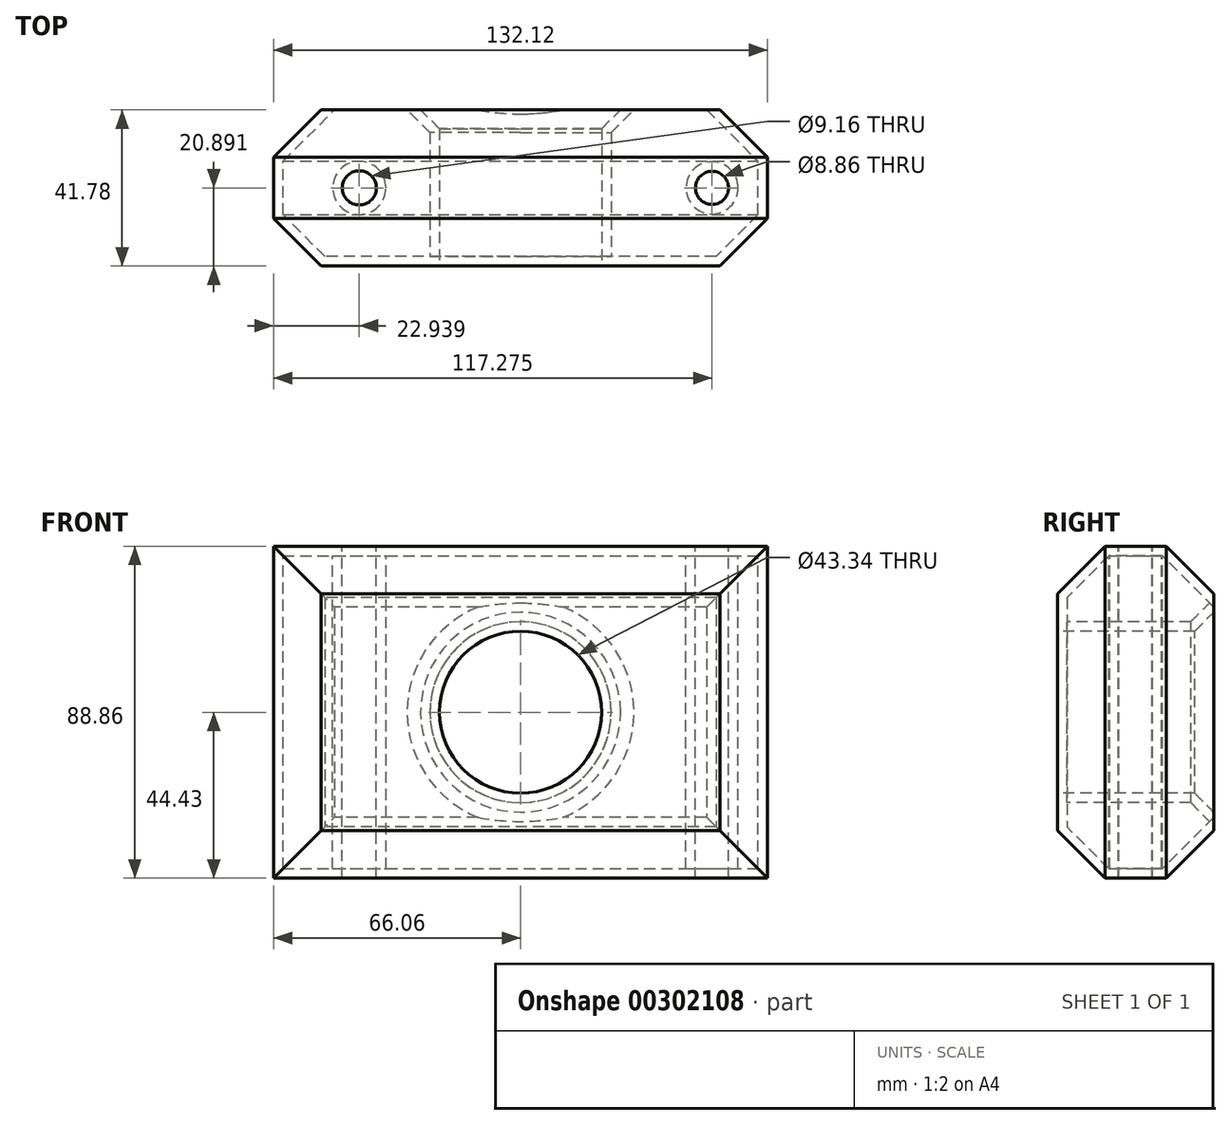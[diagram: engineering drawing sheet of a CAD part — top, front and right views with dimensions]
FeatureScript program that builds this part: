
annotation { "Feature Type Name" : "Feature", "Feature Type Description" : "" }
export const myFeature = defineFeature(function(context is Context, id is Id, definition is map)
    precondition{}
    {
        {
            var Q0;
            Q0=qCreatedBy(makeId("Front.planeOp"),FACE);
            var sketch = newSketch(context, id + "F0", { "sketchPlane" : qUnion([Q0])});
            skLineSegment(sketch, "E0.bottom", {"start": v(66.06, 44.43) * mm, "end": v(-66.06, 44.43) * mm});
            skLineSegment(sketch, "E0.top", {"start": v(66.06, -44.43) * mm, "end": v(-66.06, -44.43) * mm});
            skLineSegment(sketch, "E0.left", {"start": v(66.06, 44.43) * mm, "end": v(66.06, -44.43) * mm});
            skLineSegment(sketch, "E0.right", {"start": v(-66.06, 44.43) * mm, "end": v(-66.06, -44.43) * mm});
            skPoint(sketch, "E0.middle", {"position": v(0, 0) * mm});
            skSolve(sketch);
        }
        {
            var Q0;
            Q0=makeQuery(id+"F0.imprint","IMPRINT",FACE,{"disambiguationData":[TD([[makeQuery(id+"F0.imprint","IMPRINT",EDGE,{"derivedFrom":sQuery(id+"F0.wireOp",EDGE,"E0.bottom")}),1.0]])]});
            extrude(context, id + "F1", {"entities" : qUnion([Q0]), "depth" : 41.78 * mm});
        }
        {
            var Q0;
            Q0=makeQuery(id+"F1.opExtrude","CAP_EDGE",EDGE,{"disambiguationData":[OSD([sQuery(id+"F0.wireOp",EDGE,"E0.top")])],"isStart":false});
            var Q1;
            Q1=makeQuery(id+"F1.opExtrude","CAP_EDGE",EDGE,{"disambiguationData":[OSD([sQuery(id+"F0.wireOp",EDGE,"E0.left")])],"isStart":false});
            var Q2;
            Q2=makeQuery(id+"F1.opExtrude","CAP_EDGE",EDGE,{"disambiguationData":[OSD([sQuery(id+"F0.wireOp",EDGE,"E0.bottom")])],"isStart":false});
            var Q3;
            Q3=makeQuery(id+"F1.opExtrude","CAP_EDGE",EDGE,{"disambiguationData":[OSD([sQuery(id+"F0.wireOp",EDGE,"E0.right")])],"isStart":false});
            var Q4;
            Q4=makeQuery(id+"F1.opExtrude","CAP_EDGE",EDGE,{"disambiguationData":[OSD([sQuery(id+"F0.wireOp",EDGE,"E0.top")])],"isStart":true});
            var Q5;
            Q5=makeQuery(id+"F1.opExtrude","CAP_EDGE",EDGE,{"disambiguationData":[OSD([sQuery(id+"F0.wireOp",EDGE,"E0.left")])],"isStart":true});
            var Q6;
            Q6=makeQuery(id+"F1.opExtrude","CAP_EDGE",EDGE,{"disambiguationData":[OSD([sQuery(id+"F0.wireOp",EDGE,"E0.right")])],"isStart":true});
            var Q7;
            Q7=makeQuery(id+"F1.opExtrude","CAP_EDGE",EDGE,{"disambiguationData":[OSD([sQuery(id+"F0.wireOp",EDGE,"E0.bottom")])],"isStart":true});
            chamfer(context, id + "F2", {"entities" : qUnion([Q0, Q1, Q2, Q3, Q4, Q5, Q6, Q7]), "width" : 12.7 * mm, "tangentPropagation" : true});
        }
        {
            var Q0;
            Q0=makeQuery(id+"F1.opExtrude","CAP_FACE",FACE,{"disambiguationData":[OSD([sQuery(id+"F0.wireOp",EDGE,"E0.bottom"),sQuery(id+"F0.wireOp",EDGE,"E0.top"),sQuery(id+"F0.wireOp",EDGE,"E0.left"),sQuery(id+"F0.wireOp",EDGE,"E0.right")])],"isStart":false});
            var sketch = newSketch(context, id + "F3", { "sketchPlane" : qUnion([Q0])});
            skCircle(sketch, "E1", {"center": v(0, 0) * mm, "radius": 21.67 * mm});
            skSolve(sketch);
        }
        {
            var Q0;
            Q0=makeQuery(id+"F3.imprint","IMPRINT",FACE,{"disambiguationData":[TD([[makeQuery(id+"F3.imprint","IMPRINT",EDGE,{"derivedFrom":sQuery(id+"F3.wireOp",EDGE,"E1")}),1.0]])]});
            extrude(context, id + "F4", {"entities" : qUnion([Q0]), "operationType" : NewBodyOperationType.REMOVE, "oppositeDirection" : true, "depth" : 276.72 * mm});
        }
        {
            var Q0;
            Q0=makeQuery(id+"F4.boolean.opBoolean","INTERSECT",EDGE,{"derivedFrom":[makeQuery(id+"F1.opExtrude","CAP_FACE",FACE,{"disambiguationData":[OSD([sQuery(id+"F0.wireOp",EDGE,"E0.bottom"),sQuery(id+"F0.wireOp",EDGE,"E0.top"),sQuery(id+"F0.wireOp",EDGE,"E0.left"),sQuery(id+"F0.wireOp",EDGE,"E0.right")])],"isStart":true}),makeQuery(id+"F4.opExtrude","SWEPT_FACE",FACE,{"disambiguationData":[OSD([sQuery(id+"F3.wireOp",EDGE,"E1")])]})]});
            var Q1;
            Q1=makeQuery(id+"F4.boolean.opBoolean","COPY",EDGE,{"derivedFrom":makeQuery(id+"F4.opExtrude","CAP_EDGE",EDGE,{"disambiguationData":[OSD([sQuery(id+"F3.wireOp",EDGE,"E1")])],"isStart":true})});
            chamfer(context, id + "F5", {"entities" : qUnion([Q0, Q1]), "width" : 5.08 * mm, "tangentPropagation" : true});
        }
        {
            var Q0;
            Q0=makeQuery(id+"F1.opExtrude","SWEPT_FACE",FACE,{"disambiguationData":[OSD([sQuery(id+"F0.wireOp",EDGE,"E0.bottom")])]});
            var sketch = newSketch(context, id + "F6", { "sketchPlane" : qUnion([Q0])});
            skCircle(sketch, "E2", {"center": v(-43.12, -20.89) * mm, "radius": 4.58 * mm});
            skPoint(sketch, "E2.centerSnap0", {"position": v(-66.06, -20.89) * mm});
            skCircle(sketch, "E3", {"center": v(51.22, -20.89) * mm, "radius": 4.43 * mm});
            skPoint(sketch, "E3.centerSnap0", {"position": v(66.06, -20.89) * mm});
            skSolve(sketch);
        }
        {
            var Q0;
            Q0=makeQuery(id+"F6.imprint","IMPRINT",FACE,{"disambiguationData":[TD([[makeQuery(id+"F6.imprint","IMPRINT",EDGE,{"derivedFrom":sQuery(id+"F6.wireOp",EDGE,"E2")}),1.0]])]});
            extrude(context, id + "F7", {"entities" : qUnion([Q0]), "operationType" : NewBodyOperationType.REMOVE, "endBound" : BoundingType.THROUGH_ALL, "oppositeDirection" : true, "depth" : 25.4 * mm});
        }
        {
            var Q0;
            Q0 = qSketchRegion(id + "F6", true);
            extrude(context, id + "F8", {"entities" : qUnion([Q0]), "operationType" : NewBodyOperationType.REMOVE, "endBound" : BoundingType.THROUGH_ALL, "oppositeDirection" : true, "depth" : 25.4 * mm});
        }
        {
            var Q0;
            Q0=makeQuery(id+"F1.opExtrude","CAP_FACE",FACE,{"disambiguationData":[OSD([sQuery(id+"F0.wireOp",EDGE,"E0.bottom"),sQuery(id+"F0.wireOp",EDGE,"E0.top"),sQuery(id+"F0.wireOp",EDGE,"E0.left"),sQuery(id+"F0.wireOp",EDGE,"E0.right")])],"isStart":true});
            shell(context, id + "F9", {"entities" : qUnion([Q0]), "thickness" : 2.54 * mm});
        }
    });
